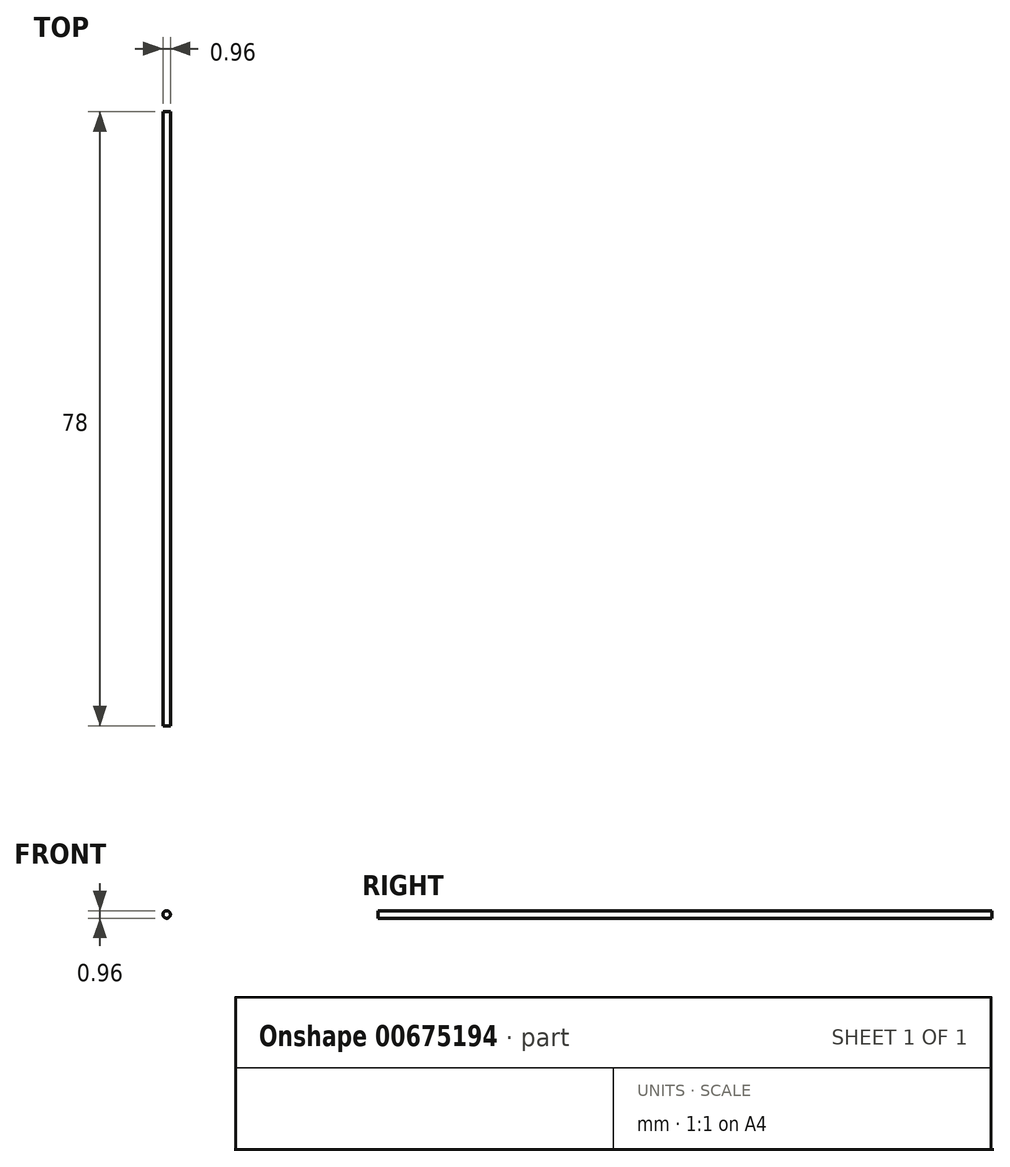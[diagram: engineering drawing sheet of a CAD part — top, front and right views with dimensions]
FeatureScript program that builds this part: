
annotation { "Feature Type Name" : "Feature", "Feature Type Description" : "" }
export const myFeature = defineFeature(function(context is Context, id is Id, definition is map)
    precondition{}
    {
        {
            var Q0;
            Q0=qCreatedBy(makeId("Front.planeOp"),FACE);
            var sketch = newSketch(context, id + "F0", { "sketchPlane" : qUnion([Q0])});
            skCircle(sketch, "E0", {"center": v(0, 0) * mm, "radius": 0.47 * mm});
            skSolve(sketch);
        }
        {
            var Q0;
            Q0 = qSketchRegion(id + "F0", true);
            extrude(context, id + "F1", {"entities" : qUnion([Q0]), "depth" : 78 * mm, "offsetDistance" : 25 * mm});
        }
    });
